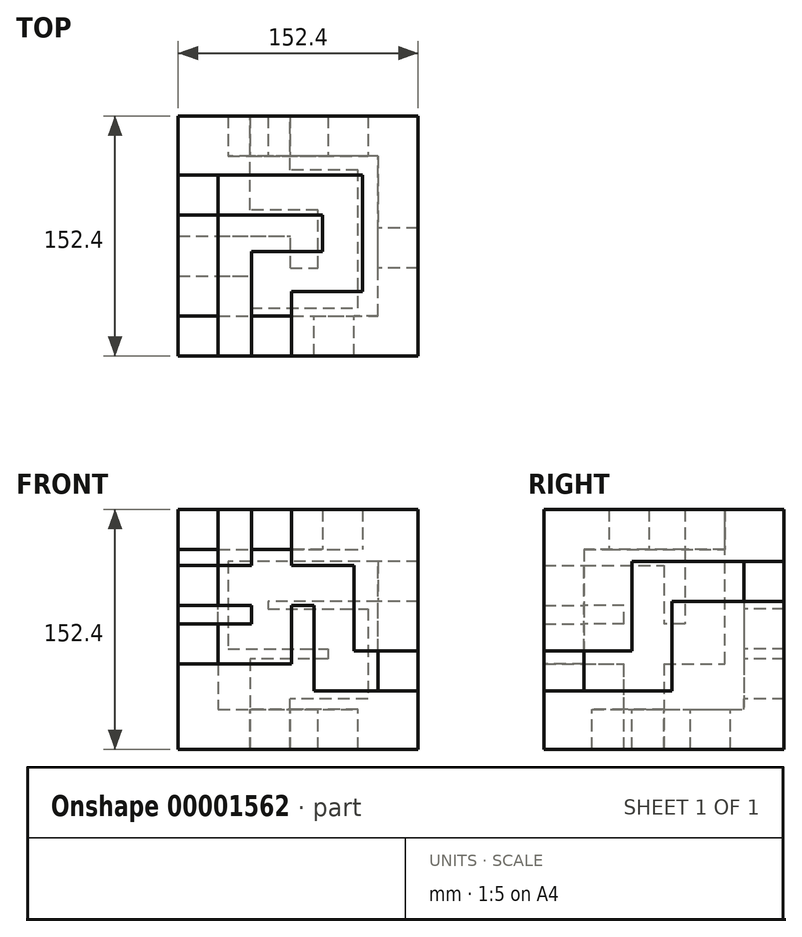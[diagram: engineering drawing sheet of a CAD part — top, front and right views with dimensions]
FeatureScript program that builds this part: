
annotation { "Feature Type Name" : "Feature", "Feature Type Description" : "" }
export const myFeature = defineFeature(function(context is Context, id is Id, definition is map)
    precondition{}
    {
        {
            var Q0;
            Q0=qCreatedBy(makeId("Top.planeOp"),FACE);
            var sketch = newSketch(context, id + "F0", { "sketchPlane" : qUnion([Q0])});
            skLineSegment(sketch, "E0.rect.bottom", {"start": v(-50.8, 50.8) * mm, "end": v(50.8, 50.8) * mm});
            skLineSegment(sketch, "E0.rect.top", {"start": v(-50.8, -50.8) * mm, "end": v(50.8, -50.8) * mm});
            skLineSegment(sketch, "E0.rect.left", {"start": v(-50.8, 50.8) * mm, "end": v(-50.8, -50.8) * mm});
            skLineSegment(sketch, "E0.rect.right", {"start": v(50.8, 50.8) * mm, "end": v(50.8, -50.8) * mm});
            skPoint(sketch, "E0.rect.middle", {"position": v(0, 0) * mm});
            skSolve(sketch);
        }
        {
            var Q0;
            Q0=makeQuery(id+"F0.imprint","IMPRINT",FACE,{"disambiguationData":[TD([[makeQuery(id+"F0.imprint","IMPRINT",EDGE,{"derivedFrom":sQuery(id+"F0.wireOp",EDGE,"E0.rect.bottom")}),-1.0]])]});
            extrude(context, id + "F1", {"entities" : qUnion([Q0]), "endBound" : BoundingType.SYMMETRIC, "depth" : 101.6 * mm});
        }
        {
            var Q0;
            Q0=makeQuery(id+"F1.opExtrude","CAP_FACE",FACE,{"disambiguationData":[OSD([sQuery(id+"F0.wireOp",EDGE,"E0.rect.bottom"),sQuery(id+"F0.wireOp",EDGE,"E0.rect.top"),sQuery(id+"F0.wireOp",EDGE,"E0.rect.left"),sQuery(id+"F0.wireOp",EDGE,"E0.rect.right")])],"isStart":false});
            var sketch = newSketch(context, id + "F2", { "sketchPlane" : qUnion([Q0])});
            skLineSegment(sketch, "E1", {"start": v(15.5, 13.25) * mm, "end": v(15.5, -9.7) * mm});
            skLineSegment(sketch, "E2", {"start": v(15.5, -9.7) * mm, "end": v(-29.46, -9.7) * mm});
            skLineSegment(sketch, "E3", {"start": v(-29.46, -9.7) * mm, "end": v(-29.46, -50.8) * mm});
            skLineSegment(sketch, "E4", {"start": v(-29.46, -50.8) * mm, "end": v(-4.06, -50.8) * mm});
            skLineSegment(sketch, "E5", {"start": v(-4.06, -50.8) * mm, "end": v(-4.06, -35.1) * mm});
            skLineSegment(sketch, "E6", {"start": v(-4.06, -35.1) * mm, "end": v(40.9, -35.1) * mm});
            skLineSegment(sketch, "E7", {"start": v(40.9, -35.1) * mm, "end": v(40.9, 38.65) * mm});
            skLineSegment(sketch, "E8.bottom", {"start": v(-50.8, 38.65) * mm, "end": v(40.9, 38.65) * mm});
            skLineSegment(sketch, "E8.top", {"start": v(-50.8, 13.25) * mm, "end": v(15.5, 13.25) * mm});
            skLineSegment(sketch, "E8.left", {"start": v(-50.8, 38.65) * mm, "end": v(-50.8, 13.25) * mm});
            skSolve(sketch);
        }
        {
            var Q0;
            Q0=makeQuery(id+"F1.opExtrude","SWEPT_FACE",FACE,{"disambiguationData":[OSD([sQuery(id+"F0.wireOp",EDGE,"E0.rect.left")])]});
            var sketch = newSketch(context, id + "F3", { "sketchPlane" : qUnion([Q0])});
            skLineSegment(sketch, "E9", {"start": v(-13.26, 50.8) * mm, "end": v(-13.26, 3.6) * mm});
            skLineSegment(sketch, "E10", {"start": v(-13.26, 3.6) * mm, "end": v(50.8, 3.6) * mm});
            skLineSegment(sketch, "E11", {"start": v(50.8, 3.6) * mm, "end": v(50.8, -21.8) * mm});
            skLineSegment(sketch, "E12", {"start": v(50.8, -21.8) * mm, "end": v(-38.66, -21.8) * mm});
            skLineSegment(sketch, "E13", {"start": v(-38.66, -21.8) * mm, "end": v(-38.66, 50.8) * mm});
            skLineSegment(sketch, "E14", {"start": v(50.8, 40.7) * mm, "end": v(0, 40.7) * mm});
            skLineSegment(sketch, "E15", {"start": v(0, 40.7) * mm, "end": v(0, -50.8) * mm});
            skLineSegment(sketch, "E16", {"start": v(0, -50.8) * mm, "end": v(25.4, -50.8) * mm});
            skLineSegment(sketch, "E17", {"start": v(25.4, -50.8) * mm, "end": v(25.4, 15.3) * mm});
            skLineSegment(sketch, "E18", {"start": v(25.4, 15.3) * mm, "end": v(50.8, 15.3) * mm});
            skSolve(sketch);
        }
        {
            var Q0;
            Q0=makeQuery(id+"F1.opExtrude","SWEPT_FACE",FACE,{"disambiguationData":[OSD([sQuery(id+"F0.wireOp",EDGE,"E0.rect.top")])]});
            var sketch = newSketch(context, id + "F4", { "sketchPlane" : qUnion([Q0])});
            skLineSegment(sketch, "E19", {"start": v(-29.46, 50.8) * mm, "end": v(-29.46, 3.6) * mm});
            skLineSegment(sketch, "E20", {"start": v(-4.06, 50.8) * mm, "end": v(-4.06, 11.87) * mm});
            skLineSegment(sketch, "E21", {"start": v(-29.46, 3.6) * mm, "end": v(-50.8, 3.6) * mm});
            skLineSegment(sketch, "E22", {"start": v(-50.8, -21.8) * mm, "end": v(-4.06, -21.8) * mm});
            skLineSegment(sketch, "E23", {"start": v(-4.06, 11.87) * mm, "end": v(-4.06, -21.8) * mm});
            skLineSegment(sketch, "E24", {"start": v(-50.8, 40.7) * mm, "end": v(10.18, 40.7) * mm});
            skLineSegment(sketch, "E25", {"start": v(-50.8, 15.3) * mm, "end": v(10.18, 15.3) * mm});
            skLineSegment(sketch, "E26", {"start": v(10.18, 15.3) * mm, "end": v(10.18, -38.9) * mm});
            skLineSegment(sketch, "E27", {"start": v(10.18, -38.9) * mm, "end": v(50.8, -38.9) * mm});
            skLineSegment(sketch, "E28", {"start": v(50.8, -38.9) * mm, "end": v(50.8, -13.5) * mm});
            skLineSegment(sketch, "E29", {"start": v(50.8, -13.5) * mm, "end": v(35.58, -13.5) * mm});
            skLineSegment(sketch, "E30", {"start": v(35.58, -13.5) * mm, "end": v(35.58, 40.7) * mm});
            skLineSegment(sketch, "E31", {"start": v(35.58, 40.7) * mm, "end": v(10.18, 40.7) * mm});
            skSolve(sketch);
        }
        {
            var Q0;
            Q0=makeQuery(id+"F1.opExtrude","CAP_FACE",FACE,{"disambiguationData":[OSD([sQuery(id+"F0.wireOp",EDGE,"E0.rect.bottom"),sQuery(id+"F0.wireOp",EDGE,"E0.rect.top"),sQuery(id+"F0.wireOp",EDGE,"E0.rect.left"),sQuery(id+"F0.wireOp",EDGE,"E0.rect.right")])],"isStart":true});
            var sketch = newSketch(context, id + "F5", { "sketchPlane" : qUnion([Q0])});
            skLineSegment(sketch, "E32", {"start": v(-50.8, 25.4) * mm, "end": v(-30.37, 25.4) * mm});
            skLineSegment(sketch, "E33", {"start": v(-50.8, 0) * mm, "end": v(-30.37, 0) * mm});
            skLineSegment(sketch, "E34", {"start": v(-4.97, 20.26) * mm, "end": v(-4.97, 0) * mm});
            skLineSegment(sketch, "E35", {"start": v(-4.97, 0) * mm, "end": v(-30.37, 0) * mm});
            skLineSegment(sketch, "E36", {"start": v(-30.37, 25.4) * mm, "end": v(-30.37, 45.66) * mm});
            skLineSegment(sketch, "E37", {"start": v(-30.37, 45.66) * mm, "end": v(37.93, 45.66) * mm});
            skLineSegment(sketch, "E38", {"start": v(37.93, 45.66) * mm, "end": v(37.93, -16.62) * mm});
            skLineSegment(sketch, "E39", {"start": v(-4.97, 20.26) * mm, "end": v(12.53, 20.26) * mm});
            skLineSegment(sketch, "E40", {"start": v(12.53, 20.26) * mm, "end": v(12.53, -16.62) * mm});
            skLineSegment(sketch, "E41", {"start": v(37.93, -16.62) * mm, "end": v(37.93, -42.02) * mm});
            skLineSegment(sketch, "E42", {"start": v(37.93, -42.02) * mm, "end": v(-5.04, -42.02) * mm});
            skLineSegment(sketch, "E43", {"start": v(-5.04, -42.02) * mm, "end": v(-5.04, -50.8) * mm});
            skLineSegment(sketch, "E44", {"start": v(12.53, -16.62) * mm, "end": v(-30.44, -16.62) * mm});
            skLineSegment(sketch, "E45", {"start": v(-30.44, -16.62) * mm, "end": v(-30.44, -50.8) * mm});
            skSolve(sketch);
        }
        {
            var Q0;
            Q0=makeQuery(id+"F1.opExtrude","SWEPT_FACE",FACE,{"disambiguationData":[OSD([sQuery(id+"F0.wireOp",EDGE,"E0.rect.right")])]});
            var sketch = newSketch(context, id + "F6", { "sketchPlane" : qUnion([Q0])});
            skLineSegment(sketch, "E46", {"start": v(-50.8, -13.49) * mm, "end": v(-40.23, -13.49) * mm});
            skLineSegment(sketch, "E47", {"start": v(-50.8, -38.89) * mm, "end": v(-40.23, -38.89) * mm});
            skLineSegment(sketch, "E48", {"start": v(50.8, 43.06) * mm, "end": v(42.8, 43.06) * mm});
            skLineSegment(sketch, "E49", {"start": v(50.8, 17.66) * mm, "end": v(42.8, 17.66) * mm});
            skLineSegment(sketch, "E50", {"start": v(-40.23, -13.49) * mm, "end": v(-20.3, -13.49) * mm});
            skLineSegment(sketch, "E51", {"start": v(-20.3, -13.49) * mm, "end": v(-20.3, 43.06) * mm});
            skLineSegment(sketch, "E52", {"start": v(-20.3, 43.06) * mm, "end": v(42.8, 43.06) * mm});
            skLineSegment(sketch, "E53", {"start": v(-40.23, -38.89) * mm, "end": v(5.1, -38.89) * mm});
            skLineSegment(sketch, "E54", {"start": v(5.1, -38.89) * mm, "end": v(5.1, 17.66) * mm});
            skLineSegment(sketch, "E55", {"start": v(5.1, 17.66) * mm, "end": v(42.8, 17.66) * mm});
            skSolve(sketch);
        }
        {
            var Q0;
            Q0=makeQuery(id+"F1.opExtrude","SWEPT_FACE",FACE,{"disambiguationData":[OSD([sQuery(id+"F0.wireOp",EDGE,"E0.rect.bottom")])]});
            var sketch = newSketch(context, id + "F7", { "sketchPlane" : qUnion([Q0])});
            skLineSegment(sketch, "E56", {"start": v(-50.8, 43.06) * mm, "end": v(-41.8, 43.06) * mm});
            skLineSegment(sketch, "E57", {"start": v(-50.8, 17.66) * mm, "end": v(-41.8, 17.66) * mm});
            skLineSegment(sketch, "E58", {"start": v(30.44, -50.8) * mm, "end": v(30.44, -44.27) * mm});
            skLineSegment(sketch, "E59", {"start": v(5.04, -50.8) * mm, "end": v(5.04, -44.27) * mm});
            skLineSegment(sketch, "E60", {"start": v(-41.8, 17.66) * mm, "end": v(19.26, 17.66) * mm});
            skLineSegment(sketch, "E61", {"start": v(19.26, 17.66) * mm, "end": v(19.26, 13.19) * mm});
            skLineSegment(sketch, "E62", {"start": v(19.26, 13.19) * mm, "end": v(-44.22, 13.19) * mm});
            skLineSegment(sketch, "E63", {"start": v(-44.22, 13.19) * mm, "end": v(-44.22, -44.27) * mm});
            skLineSegment(sketch, "E64", {"start": v(-44.22, -44.27) * mm, "end": v(5.04, -44.27) * mm});
            skLineSegment(sketch, "E65", {"start": v(-41.8, 43.06) * mm, "end": v(44.66, 43.06) * mm});
            skLineSegment(sketch, "E66", {"start": v(44.66, 43.06) * mm, "end": v(44.66, -12.21) * mm});
            skLineSegment(sketch, "E67", {"start": v(44.66, -12.21) * mm, "end": v(-18.82, -12.21) * mm});
            skLineSegment(sketch, "E68", {"start": v(-18.82, -12.21) * mm, "end": v(-18.82, -18.87) * mm});
            skLineSegment(sketch, "E69", {"start": v(-18.82, -18.87) * mm, "end": v(30.44, -18.87) * mm});
            skLineSegment(sketch, "E70", {"start": v(30.44, -18.87) * mm, "end": v(30.44, -44.27) * mm});
            skSolve(sketch);
        }
        {
            var Q0;
            {var subQ2=sQuery(id+"F7.wireOp",EDGE,"E56");Q0=makeQuery(id+"F7.imprint","IMPRINT",FACE,{"disambiguationData":[TD([[makeQuery(id+"F7.imprint","IMPRINT",EDGE,{"derivedFrom":subQ2}),1.0]])]});}
            var Q1;
            {var subQ5=sQuery(id+"F7.wireOp",EDGE,"E57");Q1=makeQuery(id+"F7.imprint","IMPRINT",FACE,{"disambiguationData":[TD([[makeQuery(id+"F7.imprint","IMPRINT",EDGE,{"derivedFrom":subQ5}),-1.0]])]});}
            extrude(context, id + "F8", {"entities" : qUnion([Q0, Q1]), "operationType" : NewBodyOperationType.ADD, "depth" : 25.4 * mm});
        }
        {
            var Q0;
            {var subQ2=sQuery(id+"F6.wireOp",EDGE,"E47");Q0=makeQuery(id+"F6.imprint","IMPRINT",FACE,{"disambiguationData":[TD([[makeQuery(id+"F6.imprint","IMPRINT",EDGE,{"derivedFrom":subQ2}),-1.0]])]});}
            var Q1;
            {var subQ2=sQuery(id+"F6.wireOp",EDGE,"E46");Q1=makeQuery(id+"F6.imprint","IMPRINT",FACE,{"disambiguationData":[TD([[makeQuery(id+"F6.imprint","IMPRINT",EDGE,{"derivedFrom":subQ2}),1.0]])]});}
            extrude(context, id + "F9", {"entities" : qUnion([Q0, Q1]), "operationType" : NewBodyOperationType.ADD, "depth" : 25.4 * mm});
        }
        {
            var Q0;
            {var subQ5=sQuery(id+"F4.wireOp",EDGE,"E22");Q0=makeQuery(id+"F4.imprint","IMPRINT",FACE,{"disambiguationData":[TD([[makeQuery(id+"F4.imprint","IMPRINT",EDGE,{"derivedFrom":subQ5}),-1.0]])]});}
            var Q1;
            {var subQ7=sQuery(id+"F4.wireOp",EDGE,"E29");Q1=makeQuery(id+"F4.imprint","IMPRINT",FACE,{"disambiguationData":[TD([[makeQuery(id+"F4.imprint","IMPRINT",EDGE,{"derivedFrom":subQ7}),-1.0]])]});}
            var Q2;
            {var subQ3=sQuery(id+"F4.wireOp",EDGE,"E21");Q2=makeQuery(id+"F4.imprint","IMPRINT",FACE,{"disambiguationData":[TD([[makeQuery(id+"F4.imprint","IMPRINT",EDGE,{"derivedFrom":subQ3}),-1.0]])]});}
            var Q3;
            {var subQ0=sQuery(id+"F0.wireOp",EDGE,"E0.rect.top");var subQ1=makeQuery(id+"F1.opExtrude","CAP_EDGE",EDGE,{"disambiguationData":[OSD([subQ0])],"isStart":false});var subQ2=sQuery(id+"F4.wireOp",EDGE,"E19");var subQ3=makeQuery(id+"F4.imprint","INTERSECT",VERTEX,{"derivedFrom":[subQ1,subQ2]});Q3=makeQuery(id+"F4.imprint","IMPRINT",FACE,{"disambiguationData":[TD([[makeQuery(id+"F4.imprint","IMPRINT",EDGE,{"disambiguationData":[TD([[subQ3,-1.0]])],"derivedFrom":subQ2}),-1.0]])]});}
            extrude(context, id + "F10", {"entities" : qUnion([Q0, Q1, Q2, Q3]), "operationType" : NewBodyOperationType.ADD, "depth" : 25.4 * mm});
        }
        {
            var Q0;
            {var subQ1=sQuery(id+"F3.wireOp",EDGE,"E18");Q0=makeQuery(id+"F3.imprint","IMPRINT",FACE,{"disambiguationData":[TD([[makeQuery(id+"F3.imprint","IMPRINT",EDGE,{"derivedFrom":subQ1}),-1.0]])]});}
            var Q1;
            {var subQ2=sQuery(id+"F3.wireOp",EDGE,"E17");var subQ6=sQuery(id+"F3.wireOp",EDGE,"E12");var subQ8=makeQuery(id+"F3.imprint","INTERSECT",VERTEX,{"derivedFrom":[subQ6,subQ2]});Q1=makeQuery(id+"F3.imprint","IMPRINT",FACE,{"disambiguationData":[TD([[makeQuery(id+"F3.imprint","IMPRINT",EDGE,{"disambiguationData":[TD([[subQ8,1.0]])],"derivedFrom":subQ2}),-1.0]])]});}
            var Q2;
            {var subQ2=sQuery(id+"F3.wireOp",EDGE,"E9");Q2=makeQuery(id+"F3.imprint","IMPRINT",FACE,{"disambiguationData":[TD([[makeQuery(id+"F3.imprint","IMPRINT",EDGE,{"derivedFrom":subQ2}),1.0]])]});}
            var Q3;
            {var subQ2=sQuery(id+"F3.wireOp",EDGE,"E13");Q3=makeQuery(id+"F3.imprint","IMPRINT",FACE,{"disambiguationData":[TD([[makeQuery(id+"F3.imprint","IMPRINT",EDGE,{"derivedFrom":subQ2}),1.0]])]});}
            extrude(context, id + "F11", {"entities" : qUnion([Q0, Q1, Q2, Q3]), "operationType" : NewBodyOperationType.ADD, "depth" : 25.4 * mm});
        }
        {
            var Q0;
            {var subQ4=sQuery(id+"F2.wireOp",EDGE,"E5");Q0=makeQuery(id+"F2.imprint","IMPRINT",FACE,{"disambiguationData":[TD([[makeQuery(id+"F2.imprint","IMPRINT",EDGE,{"derivedFrom":subQ4}),-1.0]])]});}
            var Q1;
            Q1=makeQuery(id+"F2.imprint","IMPRINT",FACE,{"disambiguationData":[TD([[makeQuery(id+"F2.imprint","IMPRINT",EDGE,{"derivedFrom":sQuery(id+"F2.wireOp",EDGE,"E1")}),-1.0]])]});
            extrude(context, id + "F12", {"entities" : qUnion([Q0, Q1]), "operationType" : NewBodyOperationType.ADD, "depth" : 25.4 * mm});
        }
        {
            var Q0;
            {var subQ1=sQuery(id+"F5.wireOp",EDGE,"E32");Q0=makeQuery(id+"F5.imprint","IMPRINT",FACE,{"disambiguationData":[TD([[makeQuery(id+"F5.imprint","IMPRINT",EDGE,{"derivedFrom":subQ1}),1.0]])]});}
            var Q1;
            {var subQ1=sQuery(id+"F5.wireOp",EDGE,"E33");Q1=makeQuery(id+"F5.imprint","IMPRINT",FACE,{"disambiguationData":[TD([[makeQuery(id+"F5.imprint","IMPRINT",EDGE,{"derivedFrom":subQ1}),-1.0]])]});}
            extrude(context, id + "F13", {"entities" : qUnion([Q0, Q1]), "operationType" : NewBodyOperationType.ADD, "depth" : 25.4 * mm});
        }
        {
            var Q0;
            Q0=makeQuery(id+"F13.opExtrude","SWEPT_FACE",FACE,{"disambiguationData":[OSD([sQuery(id+"F0.wireOp",EDGE,"E0.rect.right")])]});
            var sketch = newSketch(context, id + "F14", { "sketchPlane" : qUnion([Q0])});
            skLineSegment(sketch, "E71.bottom", {"start": v(50.8, -76.2) * mm, "end": v(-50.8, -76.2) * mm});
            skLineSegment(sketch, "E71.top", {"start": v(50.8, -50.8) * mm, "end": v(-50.8, -50.8) * mm});
            skLineSegment(sketch, "E71.left", {"start": v(50.8, -76.2) * mm, "end": v(50.8, -50.8) * mm});
            skLineSegment(sketch, "E71.right", {"start": v(-50.8, -76.2) * mm, "end": v(-50.8, -50.8) * mm});
            skSolve(sketch);
        }
        {
            var Q0;
            Q0=makeQuery(id+"F14.imprint","IMPRINT",FACE,{"disambiguationData":[TD([[makeQuery(id+"F14.imprint","IMPRINT",EDGE,{"derivedFrom":sQuery(id+"F14.wireOp",EDGE,"E71.bottom")}),-1.0]])]});
            extrude(context, id + "F15", {"entities" : qUnion([Q0]), "operationType" : NewBodyOperationType.ADD, "depth" : 25.4 * mm});
        }
        {
            var Q0;
            {var subQ0=sQuery(id+"F0.wireOp",EDGE,"E0.rect.top");var subQ1=sQuery(id+"F0.wireOp",EDGE,"E0.rect.right");var subQ2=makeQuery(id+"F1.opExtrude","SWEPT_EDGE",EDGE,{"disambiguationData":[OSD([subQ0,subQ1])]});Q0=makeQuery(id+"F10.opExtrude","SWEPT_FACE",FACE,{"disambiguationData":[OSD([subQ0,subQ1]),TDD([makeQuery(id+"F4.imprint","IMPRINT",EDGE,{"disambiguationData":[TD([[makeQuery(id+"F4.imprint","INTERSECT",VERTEX,{"derivedFrom":[subQ2,makeQuery(id+"F1.opExtrude","CAP_EDGE",EDGE,{"disambiguationData":[OSD([subQ0])],"isStart":true})]}),1.0]])],"derivedFrom":subQ2})])]});}
            var sketch = newSketch(context, id + "F16", { "sketchPlane" : qUnion([Q0])});
            skLineSegment(sketch, "E72.bottom", {"start": v(-50.8, -50.8) * mm, "end": v(-76.2, -50.8) * mm});
            skLineSegment(sketch, "E72.top", {"start": v(-50.8, -38.9) * mm, "end": v(-76.2, -38.9) * mm});
            skLineSegment(sketch, "E72.left", {"start": v(-50.8, -50.8) * mm, "end": v(-50.8, -38.9) * mm});
            skLineSegment(sketch, "E72.right", {"start": v(-76.2, -50.8) * mm, "end": v(-76.2, -38.9) * mm});
            skSolve(sketch);
        }
        {
            var Q0;
            Q0=makeQuery(id+"F16.imprint","IMPRINT",FACE,{"disambiguationData":[TD([[makeQuery(id+"F16.imprint","IMPRINT",EDGE,{"derivedFrom":sQuery(id+"F16.wireOp",EDGE,"E72.bottom")}),1.0]])]});
            extrude(context, id + "F17", {"entities" : qUnion([Q0]), "operationType" : NewBodyOperationType.ADD, "depth" : 25.4 * mm});
        }
        {
            var Q0;
            {var subQ0=sQuery(id+"F0.wireOp",EDGE,"E0.rect.top");var subQ1=sQuery(id+"F0.wireOp",EDGE,"E0.rect.right");var subQ2=makeQuery(id+"F1.opExtrude","SWEPT_EDGE",EDGE,{"disambiguationData":[OSD([subQ0,subQ1])]});var subQ3=sQuery(id+"F6.wireOp",EDGE,"E46");var subQ4=makeQuery(id+"F1.opExtrude","CAP_EDGE",EDGE,{"disambiguationData":[OSD([subQ1])],"isStart":false});var subQ8=sQuery(id+"F6.wireOp",EDGE,"E50");Q0=makeQuery(id+"F10.boolean.opBoolean","SPLIT",FACE,{"disambiguationData":[TD([makeQuery(id+"F9.opExtrude","SWEPT_FACE",FACE,{"disambiguationData":[OSD([subQ3,subQ8])]})])],"derivedFrom":makeQuery(id+"F9.boolean.opBoolean","MERGE",FACE,{"derivedFrom":[makeQuery(id+"F1.opExtrude","SWEPT_FACE",FACE,{"disambiguationData":[OSD([subQ0])]}),makeQuery(id+"F9.opExtrude","SWEPT_FACE",FACE,{"disambiguationData":[OSD([subQ0,subQ1]),TDD([makeQuery(id+"F6.imprint","IMPRINT",EDGE,{"disambiguationData":[TD([[makeQuery(id+"F6.imprint","INTERSECT",VERTEX,{"derivedFrom":[subQ2,makeQuery(id+"F1.opExtrude","CAP_EDGE",EDGE,{"disambiguationData":[OSD([subQ1])],"isStart":true})]}),1.0]])],"derivedFrom":subQ2})])]}),makeQuery(id+"F9.opExtrude","SWEPT_FACE",FACE,{"disambiguationData":[OSD([subQ0,subQ1]),TDD([makeQuery(id+"F6.imprint","IMPRINT",EDGE,{"disambiguationData":[TD([[makeQuery(id+"F6.imprint","INTERSECT",VERTEX,{"derivedFrom":[subQ2,subQ4]}),-1.0]])],"derivedFrom":subQ2})])]})]})});}
            var sketch = newSketch(context, id + "F18", { "sketchPlane" : qUnion([Q0])});
            skLineSegment(sketch, "E73.bottom", {"start": v(76.2, 50.8) * mm, "end": v(50.8, 50.8) * mm});
            skLineSegment(sketch, "E73.top", {"start": v(76.2, -13.49) * mm, "end": v(50.8, -13.49) * mm});
            skLineSegment(sketch, "E73.left", {"start": v(76.2, 50.8) * mm, "end": v(76.2, -13.49) * mm});
            skLineSegment(sketch, "E73.right", {"start": v(50.8, 50.8) * mm, "end": v(50.8, -13.49) * mm});
            skSolve(sketch);
        }
        {
            var Q0;
            Q0=makeQuery(id+"F18.imprint","IMPRINT",FACE,{"disambiguationData":[TD([[makeQuery(id+"F18.imprint","IMPRINT",EDGE,{"derivedFrom":sQuery(id+"F18.wireOp",EDGE,"E73.bottom")}),-1.0]])]});
            extrude(context, id + "F19", {"entities" : qUnion([Q0]), "operationType" : NewBodyOperationType.ADD, "depth" : 25.4 * mm});
        }
        {
            var Q0;
            {var subQ0=sQuery(id+"F0.wireOp",EDGE,"E0.rect.bottom");var subQ1=sQuery(id+"F0.wireOp",EDGE,"E0.rect.right");var subQ2=makeQuery(id+"F1.opExtrude","SWEPT_EDGE",EDGE,{"disambiguationData":[OSD([subQ0,subQ1])]});var subQ3=makeQuery(id+"F1.opExtrude","CAP_EDGE",EDGE,{"disambiguationData":[OSD([subQ1])],"isStart":true});var subQ4=makeQuery(id+"F1.opExtrude","CAP_EDGE",EDGE,{"disambiguationData":[OSD([subQ0])],"isStart":true});Q0=makeQuery(id+"F15.boolean.opBoolean","MERGE",FACE,{"derivedFrom":[makeQuery(id+"F13.boolean.opBoolean","MERGE",FACE,{"derivedFrom":[makeQuery(id+"F9.boolean.opBoolean","MERGE",FACE,{"derivedFrom":[makeQuery(id+"F1.opExtrude","SWEPT_FACE",FACE,{"disambiguationData":[OSD([subQ0])]}),makeQuery(id+"F9.opExtrude","SWEPT_FACE",FACE,{"disambiguationData":[OSD([subQ0,subQ1]),TDD([makeQuery(id+"F6.imprint","IMPRINT",EDGE,{"disambiguationData":[TD([[makeQuery(id+"F6.imprint","INTERSECT",VERTEX,{"derivedFrom":[subQ2,subQ3]}),1.0]])],"derivedFrom":subQ2})])]})]}),makeQuery(id+"F13.opExtrude","SWEPT_FACE",FACE,{"disambiguationData":[OSD([subQ0]),TDD([makeQuery(id+"F5.imprint","IMPRINT",EDGE,{"disambiguationData":[TD([[makeQuery(id+"F5.imprint","INTERSECT",VERTEX,{"derivedFrom":[subQ4,subQ3]}),1.0]])],"derivedFrom":subQ4})])]})]}),makeQuery(id+"F15.opExtrude","SWEPT_FACE",FACE,{"disambiguationData":[OSD([sQuery(id+"F14.wireOp",EDGE,"E71.left")])]})]});}
            var sketch = newSketch(context, id + "F20", { "sketchPlane" : qUnion([Q0])});
            skLineSegment(sketch, "E74.bottom", {"start": v(-76.2, 17.66) * mm, "end": v(-50.8, 17.66) * mm});
            skLineSegment(sketch, "E74.top", {"start": v(-76.2, -76.2) * mm, "end": v(-50.8, -76.2) * mm});
            skLineSegment(sketch, "E74.left", {"start": v(-76.2, 17.66) * mm, "end": v(-76.2, -76.2) * mm});
            skLineSegment(sketch, "E74.right", {"start": v(-50.8, 17.66) * mm, "end": v(-50.8, -50.8) * mm});
            skLineSegment(sketch, "E75.bottom", {"start": v(-50.8, -50.8) * mm, "end": v(5.04, -50.8) * mm});
            skLineSegment(sketch, "E75.top", {"start": v(-50.8, -76.2) * mm, "end": v(5.04, -76.2) * mm});
            skLineSegment(sketch, "E75.right", {"start": v(5.04, -50.8) * mm, "end": v(5.04, -76.2) * mm});
            skSolve(sketch);
        }
        {
            var Q0;
            {var subQ7=sQuery(id+"F20.wireOp",EDGE,"E74.bottom");Q0=makeQuery(id+"F20.imprint","IMPRINT",FACE,{"disambiguationData":[TD([[makeQuery(id+"F20.imprint","IMPRINT",EDGE,{"derivedFrom":subQ7}),-1.0]])]});}
            extrude(context, id + "F21", {"entities" : qUnion([Q0]), "operationType" : NewBodyOperationType.ADD, "depth" : 25.4 * mm});
        }
        {
            var Q0;
            {var subQ0=sQuery(id+"F0.wireOp",EDGE,"E0.rect.bottom");var subQ1=sQuery(id+"F0.wireOp",EDGE,"E0.rect.top");var subQ2=sQuery(id+"F0.wireOp",EDGE,"E0.rect.left");var subQ3=sQuery(id+"F0.wireOp",EDGE,"E0.rect.right");var subQ4=makeQuery(id+"F1.opExtrude","CAP_FACE",FACE,{"disambiguationData":[OSD([subQ0,subQ1,subQ2,subQ3])],"isStart":false});var subQ5=makeQuery(id+"F1.opExtrude","CAP_EDGE",EDGE,{"disambiguationData":[OSD([subQ0])],"isStart":false});var subQ6=makeQuery(id+"F8.opExtrude","SWEPT_FACE",FACE,{"disambiguationData":[OSD([subQ0]),TDD([makeQuery(id+"F7.imprint","IMPRINT",EDGE,{"derivedFrom":subQ5})])]});var subQ7=makeQuery(id+"F1.opExtrude","CAP_EDGE",EDGE,{"disambiguationData":[OSD([subQ3])],"isStart":false});var subQ8=makeQuery(id+"F9.opExtrude","SWEPT_FACE",FACE,{"disambiguationData":[OSD([subQ3]),TDD([makeQuery(id+"F6.imprint","IMPRINT",EDGE,{"derivedFrom":subQ7})])]});var subQ9=makeQuery(id+"F1.opExtrude","CAP_EDGE",EDGE,{"disambiguationData":[OSD([subQ1])],"isStart":false});var subQ11=makeQuery(id+"F10.opExtrude","SWEPT_FACE",FACE,{"disambiguationData":[OSD([subQ1]),TDD([makeQuery(id+"F4.imprint","IMPRINT",EDGE,{"disambiguationData":[TD([[makeQuery(id+"F4.imprint","INTERSECT",VERTEX,{"derivedFrom":[subQ9,sQuery(id+"F4.wireOp",EDGE,"E19")]}),1.0]])],"derivedFrom":subQ9})])]});var subQ12=sQuery(id+"F4.wireOp",EDGE,"E20");var subQ15=makeQuery(id+"F10.opExtrude","SWEPT_FACE",FACE,{"disambiguationData":[OSD([subQ1]),TDD([makeQuery(id+"F4.imprint","IMPRINT",EDGE,{"disambiguationData":[TD([[makeQuery(id+"F4.imprint","INTERSECT",VERTEX,{"derivedFrom":[subQ9,subQ12]}),-1.0]])],"derivedFrom":subQ9})])]});var subQ16=makeQuery(id+"F1.opExtrude","CAP_EDGE",EDGE,{"disambiguationData":[OSD([subQ2])],"isStart":false});var subQ17=makeQuery(id+"F11.opExtrude","SWEPT_FACE",FACE,{"disambiguationData":[OSD([subQ2]),TDD([makeQuery(id+"F3.imprint","IMPRINT",EDGE,{"disambiguationData":[TD([[makeQuery(id+"F3.imprint","INTERSECT",VERTEX,{"derivedFrom":[subQ16,sQuery(id+"F3.wireOp",EDGE,"E13")]}),1.0]])],"derivedFrom":subQ16})])]});var subQ18=makeQuery(id+"F11.opExtrude","SWEPT_FACE",FACE,{"disambiguationData":[OSD([subQ2]),TDD([makeQuery(id+"F3.imprint","IMPRINT",EDGE,{"disambiguationData":[TD([[makeQuery(id+"F3.imprint","INTERSECT",VERTEX,{"derivedFrom":[subQ16,sQuery(id+"F3.wireOp",EDGE,"E9")]}),-1.0]])],"derivedFrom":subQ16})])]});var subQ19=makeQuery(id+"F11.boolean.opBoolean","MERGE",FACE,{"derivedFrom":[makeQuery(id+"F10.boolean.opBoolean","MERGE",FACE,{"derivedFrom":[makeQuery(id+"F9.boolean.opBoolean","MERGE",FACE,{"derivedFrom":[makeQuery(id+"F8.boolean.opBoolean","MERGE",FACE,{"derivedFrom":[subQ4,subQ6]}),subQ8]}),subQ11,subQ15]}),subQ17,subQ18]});var subQ21=sQuery(id+"F6.wireOp",EDGE,"E46");var subQ25=sQuery(id+"F6.wireOp",EDGE,"E48");var subQ30=sQuery(id+"F4.wireOp",EDGE,"E29");Q0=makeQuery(id+"F19.boolean.opBoolean","MERGE",FACE,{"derivedFrom":[makeQuery(id+"F12.boolean.opBoolean","SPLIT",FACE,{"disambiguationData":[TD([makeQuery(id+"F9.opExtrude","CAP_FACE",FACE,{"disambiguationData":[OSD([subQ0,subQ1,subQ3,subQ21,subQ25,sQuery(id+"F6.wireOp",EDGE,"E50"),sQuery(id+"F6.wireOp",EDGE,"E51"),sQuery(id+"F6.wireOp",EDGE,"E52")])],"isStart":false})])],"derivedFrom":subQ19}),makeQuery(id+"F12.boolean.opBoolean","SPLIT",FACE,{"disambiguationData":[TD([makeQuery(id+"F10.opExtrude","CAP_FACE",FACE,{"disambiguationData":[OSD([subQ1,subQ3,subQ12,sQuery(id+"F4.wireOp",EDGE,"E24"),subQ30,sQuery(id+"F4.wireOp",EDGE,"E30"),sQuery(id+"F4.wireOp",EDGE,"E31")])],"isStart":false})])],"derivedFrom":subQ19}),makeQuery(id+"F19.opExtrude","SWEPT_FACE",FACE,{"disambiguationData":[OSD([sQuery(id+"F18.wireOp",EDGE,"E73.bottom")])]})]});}
            var sketch = newSketch(context, id + "F22", { "sketchPlane" : qUnion([Q0])});
            skLineSegment(sketch, "E76", {"start": v(50.8, 50.8) * mm, "end": v(76.2, 50.8) * mm});
            skLineSegment(sketch, "E77", {"start": v(76.2, 50.8) * mm, "end": v(76.2, -76.2) * mm});
            skLineSegment(sketch, "E78", {"start": v(76.2, -76.2) * mm, "end": v(-4.06, -76.2) * mm});
            skLineSegment(sketch, "E79", {"start": v(-4.06, -76.2) * mm, "end": v(-4.06, -50.8) * mm});
            skLineSegment(sketch, "E80", {"start": v(-4.06, -50.8) * mm, "end": v(50.8, -50.8) * mm});
            skLineSegment(sketch, "E81", {"start": v(50.8, -50.8) * mm, "end": v(50.8, 50.8) * mm});
            skSolve(sketch);
        }
        {
            var Q0;
            Q0=makeQuery(id+"F22.imprint","IMPRINT",FACE,{"disambiguationData":[TD([[makeQuery(id+"F22.imprint","IMPRINT",EDGE,{"derivedFrom":sQuery(id+"F22.wireOp",EDGE,"E76")}),1.0]])]});
            extrude(context, id + "F23", {"entities" : qUnion([Q0]), "operationType" : NewBodyOperationType.ADD, "depth" : 25.4 * mm});
        }
        {
            var Q0;
            {var subQ0=sQuery(id+"F0.wireOp",EDGE,"E0.rect.bottom");var subQ1=sQuery(id+"F0.wireOp",EDGE,"E0.rect.right");var subQ2=makeQuery(id+"F1.opExtrude","SWEPT_EDGE",EDGE,{"disambiguationData":[OSD([subQ0,subQ1])]});Q0=makeQuery(id+"F23.boolean.opBoolean","MERGE",FACE,{"derivedFrom":[makeQuery(id+"F9.opExtrude","SWEPT_FACE",FACE,{"disambiguationData":[OSD([subQ0,subQ1]),TDD([makeQuery(id+"F6.imprint","IMPRINT",EDGE,{"disambiguationData":[TD([[makeQuery(id+"F6.imprint","INTERSECT",VERTEX,{"derivedFrom":[subQ2,makeQuery(id+"F1.opExtrude","CAP_EDGE",EDGE,{"disambiguationData":[OSD([subQ1])],"isStart":false})]}),-1.0]])],"derivedFrom":subQ2})])]}),makeQuery(id+"F12.opExtrude","SWEPT_FACE",FACE,{"disambiguationData":[OSD([subQ0])]}),makeQuery(id+"F23.opExtrude","SWEPT_FACE",FACE,{"disambiguationData":[OSD([sQuery(id+"F22.wireOp",EDGE,"E76")])]})]});}
            var sketch = newSketch(context, id + "F24", { "sketchPlane" : qUnion([Q0])});
            skLineSegment(sketch, "E82", {"start": v(50.8, 76.2) * mm, "end": v(-76.2, 76.2) * mm});
            skLineSegment(sketch, "E83", {"start": v(-76.2, 76.2) * mm, "end": v(-76.2, 43.06) * mm});
            skLineSegment(sketch, "E84", {"start": v(-76.2, 43.06) * mm, "end": v(-50.8, 43.06) * mm});
            skLineSegment(sketch, "E85", {"start": v(-50.8, 43.06) * mm, "end": v(-50.8, 50.8) * mm});
            skLineSegment(sketch, "E86", {"start": v(-50.8, 50.8) * mm, "end": v(50.8, 50.8) * mm});
            skLineSegment(sketch, "E87", {"start": v(50.8, 50.8) * mm, "end": v(50.8, 76.2) * mm});
            skSolve(sketch);
        }
        {
            var Q0;
            Q0=makeQuery(id+"F24.imprint","IMPRINT",FACE,{"disambiguationData":[TD([[makeQuery(id+"F24.imprint","IMPRINT",EDGE,{"derivedFrom":sQuery(id+"F24.wireOp",EDGE,"E82")}),1.0]])]});
            extrude(context, id + "F25", {"entities" : qUnion([Q0]), "operationType" : NewBodyOperationType.ADD, "depth" : 25.4 * mm});
        }
        {
            var Q0;
            {var subQ0=sQuery(id+"F0.wireOp",EDGE,"E0.rect.top");var subQ1=sQuery(id+"F0.wireOp",EDGE,"E0.rect.right");var subQ2=makeQuery(id+"F1.opExtrude","SWEPT_EDGE",EDGE,{"disambiguationData":[OSD([subQ0,subQ1])]});var subQ4=makeQuery(id+"F1.opExtrude","CAP_EDGE",EDGE,{"disambiguationData":[OSD([subQ1])],"isStart":true});var subQ5=makeQuery(id+"F1.opExtrude","CAP_EDGE",EDGE,{"disambiguationData":[OSD([subQ1])],"isStart":false});var subQ11=sQuery(id+"F0.wireOp",EDGE,"E0.rect.left");var subQ12=makeQuery(id+"F1.opExtrude","SWEPT_EDGE",EDGE,{"disambiguationData":[OSD([subQ0,subQ11])]});var subQ24=makeQuery(id+"F1.opExtrude","SWEPT_FACE",FACE,{"disambiguationData":[OSD([subQ11])]});var subQ44=sQuery(id+"F14.wireOp",EDGE,"E71.right");var subQ45=sQuery(id+"F14.wireOp",EDGE,"E71.bottom");Q0=makeQuery(id+"F17.boolean.opBoolean","SPLIT",FACE,{"disambiguationData":[TD([makeQuery(id+"F15.opExtrude","SWEPT_FACE",FACE,{"disambiguationData":[OSD([subQ45])]})])],"derivedFrom":makeQuery(id+"F15.boolean.opBoolean","MERGE",FACE,{"derivedFrom":[makeQuery(id+"F11.boolean.opBoolean","MERGE",FACE,{"derivedFrom":[makeQuery(id+"F10.boolean.opBoolean","SPLIT",FACE,{"disambiguationData":[TD([subQ24])],"derivedFrom":makeQuery(id+"F9.boolean.opBoolean","MERGE",FACE,{"derivedFrom":[makeQuery(id+"F1.opExtrude","SWEPT_FACE",FACE,{"disambiguationData":[OSD([subQ0])]}),makeQuery(id+"F9.opExtrude","SWEPT_FACE",FACE,{"disambiguationData":[OSD([subQ0,subQ1]),TDD([makeQuery(id+"F6.imprint","IMPRINT",EDGE,{"disambiguationData":[TD([[makeQuery(id+"F6.imprint","INTERSECT",VERTEX,{"derivedFrom":[subQ2,subQ4]}),1.0]])],"derivedFrom":subQ2})])]}),makeQuery(id+"F9.opExtrude","SWEPT_FACE",FACE,{"disambiguationData":[OSD([subQ0,subQ1]),TDD([makeQuery(id+"F6.imprint","IMPRINT",EDGE,{"disambiguationData":[TD([[makeQuery(id+"F6.imprint","INTERSECT",VERTEX,{"derivedFrom":[subQ2,subQ5]}),-1.0]])],"derivedFrom":subQ2})])]})]})}),makeQuery(id+"F11.opExtrude","SWEPT_FACE",FACE,{"disambiguationData":[OSD([subQ0,subQ11]),TDD([makeQuery(id+"F3.imprint","IMPRINT",EDGE,{"disambiguationData":[TD([[makeQuery(id+"F3.imprint","INTERSECT",VERTEX,{"derivedFrom":[subQ12,sQuery(id+"F3.wireOp",EDGE,"E18")]}),-1.0]])],"derivedFrom":subQ12})])]})]}),makeQuery(id+"F13.opExtrude","SWEPT_FACE",FACE,{"disambiguationData":[OSD([subQ0])]}),makeQuery(id+"F15.opExtrude","SWEPT_FACE",FACE,{"disambiguationData":[OSD([subQ44])]})]})});}
            var sketch = newSketch(context, id + "F26", { "sketchPlane" : qUnion([Q0])});
            skLineSegment(sketch, "E88.bottom", {"start": v(76.2, -76.2) * mm, "end": v(-50.8, -76.2) * mm});
            skLineSegment(sketch, "E88.top", {"start": v(76.2, -50.8) * mm, "end": v(-50.8, -50.8) * mm});
            skLineSegment(sketch, "E88.left", {"start": v(76.2, -76.2) * mm, "end": v(76.2, -50.8) * mm});
            skLineSegment(sketch, "E88.right", {"start": v(-50.8, -76.2) * mm, "end": v(-50.8, -50.8) * mm});
            skSolve(sketch);
        }
        {
            var Q0;
            Q0=makeQuery(id+"F26.imprint","IMPRINT",FACE,{"disambiguationData":[TD([[makeQuery(id+"F26.imprint","IMPRINT",EDGE,{"derivedFrom":sQuery(id+"F26.wireOp",EDGE,"E88.bottom")}),1.0]])]});
            extrude(context, id + "F27", {"entities" : qUnion([Q0]), "operationType" : NewBodyOperationType.ADD, "depth" : 25.4 * mm});
        }
        {
            var Q0;
            {var subQ0=sQuery(id+"F0.wireOp",EDGE,"E0.rect.left");var subQ1=makeQuery(id+"F1.opExtrude","CAP_EDGE",EDGE,{"disambiguationData":[OSD([subQ0])],"isStart":true});Q0=makeQuery(id+"F13.opExtrude","SWEPT_FACE",FACE,{"disambiguationData":[OSD([subQ0]),TDD([makeQuery(id+"F5.imprint","IMPRINT",EDGE,{"disambiguationData":[TD([[makeQuery(id+"F5.imprint","INTERSECT",VERTEX,{"derivedFrom":[makeQuery(id+"F1.opExtrude","CAP_EDGE",EDGE,{"disambiguationData":[OSD([sQuery(id+"F0.wireOp",EDGE,"E0.rect.bottom")])],"isStart":true}),subQ1]}),-1.0]])],"derivedFrom":subQ1})])]});}
            var sketch = newSketch(context, id + "F28", { "sketchPlane" : qUnion([Q0])});
            skLineSegment(sketch, "E89.bottom", {"start": v(-50.8, -76.2) * mm, "end": v(0, -76.2) * mm});
            skLineSegment(sketch, "E89.top", {"start": v(-50.8, -50.8) * mm, "end": v(0, -50.8) * mm});
            skLineSegment(sketch, "E89.left", {"start": v(-50.8, -76.2) * mm, "end": v(-50.8, -50.8) * mm});
            skLineSegment(sketch, "E89.right", {"start": v(0, -76.2) * mm, "end": v(0, -50.8) * mm});
            skSolve(sketch);
        }
        {
            var Q0;
            Q0=makeQuery(id+"F28.imprint","IMPRINT",FACE,{"disambiguationData":[TD([[makeQuery(id+"F28.imprint","IMPRINT",EDGE,{"derivedFrom":sQuery(id+"F28.wireOp",EDGE,"E89.bottom")}),1.0]])]});
            extrude(context, id + "F29", {"entities" : qUnion([Q0]), "operationType" : NewBodyOperationType.ADD, "depth" : 25.4 * mm});
        }
        {
            var Q0;
            {var subQ0=sQuery(id+"F0.wireOp",EDGE,"E0.rect.bottom");var subQ1=sQuery(id+"F0.wireOp",EDGE,"E0.rect.left");var subQ2=makeQuery(id+"F1.opExtrude","CAP_EDGE",EDGE,{"disambiguationData":[OSD([subQ0])],"isStart":true});Q0=makeQuery(id+"F29.boolean.opBoolean","MERGE",FACE,{"derivedFrom":[makeQuery(id+"F11.opExtrude","SWEPT_FACE",FACE,{"disambiguationData":[OSD([subQ0,subQ1])]}),makeQuery(id+"F13.opExtrude","SWEPT_FACE",FACE,{"disambiguationData":[OSD([subQ0]),TDD([makeQuery(id+"F5.imprint","IMPRINT",EDGE,{"disambiguationData":[TD([[makeQuery(id+"F5.imprint","INTERSECT",VERTEX,{"derivedFrom":[subQ2,makeQuery(id+"F1.opExtrude","CAP_EDGE",EDGE,{"disambiguationData":[OSD([subQ1])],"isStart":true})]}),-1.0]])],"derivedFrom":subQ2})])]}),makeQuery(id+"F29.opExtrude","SWEPT_FACE",FACE,{"disambiguationData":[OSD([sQuery(id+"F28.wireOp",EDGE,"E89.left")])]})]});}
            var sketch = newSketch(context, id + "F30", { "sketchPlane" : qUnion([Q0])});
            skLineSegment(sketch, "E90", {"start": v(30.44, -76.2) * mm, "end": v(30.44, -50.8) * mm});
            skLineSegment(sketch, "E91", {"start": v(30.44, -50.8) * mm, "end": v(50.8, -50.8) * mm});
            skLineSegment(sketch, "E92", {"start": v(50.8, -50.8) * mm, "end": v(50.8, 50.8) * mm});
            skLineSegment(sketch, "E93", {"start": v(50.8, 50.8) * mm, "end": v(76.2, 50.8) * mm});
            skLineSegment(sketch, "E94", {"start": v(76.2, 50.8) * mm, "end": v(76.2, -76.2) * mm});
            skLineSegment(sketch, "E95", {"start": v(76.2, -76.2) * mm, "end": v(30.44, -76.2) * mm});
            skSolve(sketch);
        }
        {
            var Q0;
            Q0=makeQuery(id+"F30.imprint","IMPRINT",FACE,{"disambiguationData":[TD([[makeQuery(id+"F30.imprint","IMPRINT",EDGE,{"derivedFrom":sQuery(id+"F30.wireOp",EDGE,"E90")}),-1.0]])]});
            extrude(context, id + "F31", {"entities" : qUnion([Q0]), "operationType" : NewBodyOperationType.ADD, "depth" : 25.4 * mm});
        }
        {
            var Q0;
            {var subQ0=sQuery(id+"F0.wireOp",EDGE,"E0.rect.bottom");var subQ1=sQuery(id+"F0.wireOp",EDGE,"E0.rect.top");var subQ2=sQuery(id+"F0.wireOp",EDGE,"E0.rect.left");var subQ3=sQuery(id+"F0.wireOp",EDGE,"E0.rect.right");var subQ4=makeQuery(id+"F1.opExtrude","CAP_FACE",FACE,{"disambiguationData":[OSD([subQ0,subQ1,subQ2,subQ3])],"isStart":false});var subQ5=makeQuery(id+"F1.opExtrude","CAP_EDGE",EDGE,{"disambiguationData":[OSD([subQ0])],"isStart":false});var subQ6=makeQuery(id+"F8.opExtrude","SWEPT_FACE",FACE,{"disambiguationData":[OSD([subQ0]),TDD([makeQuery(id+"F7.imprint","IMPRINT",EDGE,{"derivedFrom":subQ5})])]});var subQ7=makeQuery(id+"F9.opExtrude","SWEPT_FACE",FACE,{"disambiguationData":[OSD([subQ3]),TDD([makeQuery(id+"F6.imprint","IMPRINT",EDGE,{"derivedFrom":makeQuery(id+"F1.opExtrude","CAP_EDGE",EDGE,{"disambiguationData":[OSD([subQ3])],"isStart":false})})])]});var subQ8=makeQuery(id+"F1.opExtrude","CAP_EDGE",EDGE,{"disambiguationData":[OSD([subQ1])],"isStart":false});var subQ11=makeQuery(id+"F10.opExtrude","SWEPT_FACE",FACE,{"disambiguationData":[OSD([subQ1]),TDD([makeQuery(id+"F4.imprint","IMPRINT",EDGE,{"disambiguationData":[TD([[makeQuery(id+"F4.imprint","INTERSECT",VERTEX,{"derivedFrom":[subQ8,sQuery(id+"F4.wireOp",EDGE,"E19")]}),1.0]])],"derivedFrom":subQ8})])]});var subQ12=makeQuery(id+"F10.opExtrude","SWEPT_FACE",FACE,{"disambiguationData":[OSD([subQ1]),TDD([makeQuery(id+"F4.imprint","IMPRINT",EDGE,{"disambiguationData":[TD([[makeQuery(id+"F4.imprint","INTERSECT",VERTEX,{"derivedFrom":[subQ8,sQuery(id+"F4.wireOp",EDGE,"E20")]}),-1.0]])],"derivedFrom":subQ8})])]});var subQ13=makeQuery(id+"F1.opExtrude","CAP_EDGE",EDGE,{"disambiguationData":[OSD([subQ2])],"isStart":false});var subQ14=sQuery(id+"F3.wireOp",EDGE,"E13");var subQ15=makeQuery(id+"F11.opExtrude","SWEPT_FACE",FACE,{"disambiguationData":[OSD([subQ2]),TDD([makeQuery(id+"F3.imprint","IMPRINT",EDGE,{"disambiguationData":[TD([[makeQuery(id+"F3.imprint","INTERSECT",VERTEX,{"derivedFrom":[subQ13,subQ14]}),1.0]])],"derivedFrom":subQ13})])]});var subQ16=makeQuery(id+"F11.opExtrude","SWEPT_FACE",FACE,{"disambiguationData":[OSD([subQ2]),TDD([makeQuery(id+"F3.imprint","IMPRINT",EDGE,{"disambiguationData":[TD([[makeQuery(id+"F3.imprint","INTERSECT",VERTEX,{"derivedFrom":[subQ13,sQuery(id+"F3.wireOp",EDGE,"E9")]}),-1.0]])],"derivedFrom":subQ13})])]});Q0=makeQuery(id+"F31.boolean.opBoolean","MERGE",FACE,{"derivedFrom":[makeQuery(id+"F12.boolean.opBoolean","SPLIT",FACE,{"disambiguationData":[TD([makeQuery(id+"F11.opExtrude","SWEPT_FACE",FACE,{"disambiguationData":[OSD([subQ14])]})])],"derivedFrom":makeQuery(id+"F11.boolean.opBoolean","MERGE",FACE,{"derivedFrom":[makeQuery(id+"F10.boolean.opBoolean","MERGE",FACE,{"derivedFrom":[makeQuery(id+"F9.boolean.opBoolean","MERGE",FACE,{"derivedFrom":[makeQuery(id+"F8.boolean.opBoolean","MERGE",FACE,{"derivedFrom":[subQ4,subQ6]}),subQ7]}),subQ11,subQ12]}),subQ15,subQ16]})}),makeQuery(id+"F31.opExtrude","SWEPT_FACE",FACE,{"disambiguationData":[OSD([sQuery(id+"F30.wireOp",EDGE,"E93")])]})]});}
            var sketch = newSketch(context, id + "F32", { "sketchPlane" : qUnion([Q0])});
            skLineSegment(sketch, "E96.bottom", {"start": v(-76.2, 76.2) * mm, "end": v(-50.8, 76.2) * mm});
            skLineSegment(sketch, "E96.top", {"start": v(-76.2, 38.66) * mm, "end": v(-50.8, 38.66) * mm});
            skLineSegment(sketch, "E96.left", {"start": v(-76.2, 76.2) * mm, "end": v(-76.2, 38.66) * mm});
            skLineSegment(sketch, "E96.right", {"start": v(-50.8, 76.2) * mm, "end": v(-50.8, 38.66) * mm});
            skSolve(sketch);
        }
        {
            var Q0;
            Q0=makeQuery(id+"F32.imprint","IMPRINT",FACE,{"disambiguationData":[TD([[makeQuery(id+"F32.imprint","IMPRINT",EDGE,{"derivedFrom":sQuery(id+"F32.wireOp",EDGE,"E96.bottom")}),-1.0]])]});
            extrude(context, id + "F33", {"entities" : qUnion([Q0]), "operationType" : NewBodyOperationType.ADD, "depth" : 25.4 * mm});
        }
        {
            var Q0;
            {var subQ0=sQuery(id+"F0.wireOp",EDGE,"E0.rect.top");var subQ1=sQuery(id+"F0.wireOp",EDGE,"E0.rect.left");var subQ2=makeQuery(id+"F1.opExtrude","SWEPT_EDGE",EDGE,{"disambiguationData":[OSD([subQ0,subQ1])]});Q0=makeQuery(id+"F11.opExtrude","SWEPT_FACE",FACE,{"disambiguationData":[OSD([subQ0,subQ1]),TDD([makeQuery(id+"F3.imprint","IMPRINT",EDGE,{"disambiguationData":[TD([[makeQuery(id+"F3.imprint","INTERSECT",VERTEX,{"derivedFrom":[subQ2,makeQuery(id+"F1.opExtrude","CAP_EDGE",EDGE,{"disambiguationData":[OSD([subQ1])],"isStart":true})]}),1.0]])],"derivedFrom":subQ2})])]});}
            var sketch = newSketch(context, id + "F34", { "sketchPlane" : qUnion([Q0])});
            skLineSegment(sketch, "E97.bottom", {"start": v(-76.2, -50.8) * mm, "end": v(-50.8, -50.8) * mm});
            skLineSegment(sketch, "E97.top", {"start": v(-76.2, -21.8) * mm, "end": v(-50.8, -21.8) * mm});
            skLineSegment(sketch, "E97.left", {"start": v(-76.2, -50.8) * mm, "end": v(-76.2, -21.8) * mm});
            skLineSegment(sketch, "E97.right", {"start": v(-50.8, -50.8) * mm, "end": v(-50.8, -21.8) * mm});
            skSolve(sketch);
        }
        {
            var Q0;
            Q0=makeQuery(id+"F34.imprint","IMPRINT",FACE,{"disambiguationData":[TD([[makeQuery(id+"F34.imprint","IMPRINT",EDGE,{"derivedFrom":sQuery(id+"F34.wireOp",EDGE,"E97.bottom")}),1.0]])]});
            extrude(context, id + "F35", {"entities" : qUnion([Q0]), "operationType" : NewBodyOperationType.ADD, "depth" : 25.4 * mm});
        }
        {
            var Q0;
            {var subQ0=sQuery(id+"F0.wireOp",EDGE,"E0.rect.bottom");var subQ1=sQuery(id+"F0.wireOp",EDGE,"E0.rect.top");var subQ2=sQuery(id+"F0.wireOp",EDGE,"E0.rect.left");var subQ3=sQuery(id+"F0.wireOp",EDGE,"E0.rect.right");var subQ4=makeQuery(id+"F1.opExtrude","CAP_FACE",FACE,{"disambiguationData":[OSD([subQ0,subQ1,subQ2,subQ3])],"isStart":true});var subQ5=makeQuery(id+"F1.opExtrude","CAP_EDGE",EDGE,{"disambiguationData":[OSD([subQ0])],"isStart":true});var subQ6=makeQuery(id+"F1.opExtrude","SWEPT_EDGE",EDGE,{"disambiguationData":[OSD([subQ0,subQ2])]});var subQ7=makeQuery(id+"F8.opExtrude","SWEPT_FACE",FACE,{"disambiguationData":[OSD([subQ0]),TDD([makeQuery(id+"F7.imprint","IMPRINT",EDGE,{"disambiguationData":[TD([[makeQuery(id+"F7.imprint","INTERSECT",VERTEX,{"derivedFrom":[subQ5,sQuery(id+"F7.wireOp",EDGE,"E58")]}),1.0]])],"derivedFrom":subQ5})])]});var subQ8=makeQuery(id+"F8.opExtrude","SWEPT_FACE",FACE,{"disambiguationData":[OSD([subQ0]),TDD([makeQuery(id+"F7.imprint","IMPRINT",EDGE,{"disambiguationData":[TD([[makeQuery(id+"F7.imprint","INTERSECT",VERTEX,{"derivedFrom":[subQ5,sQuery(id+"F7.wireOp",EDGE,"E59")]}),-1.0]])],"derivedFrom":subQ5})])]});var subQ9=makeQuery(id+"F9.opExtrude","SWEPT_FACE",FACE,{"disambiguationData":[OSD([subQ3]),TDD([makeQuery(id+"F6.imprint","IMPRINT",EDGE,{"derivedFrom":makeQuery(id+"F1.opExtrude","CAP_EDGE",EDGE,{"disambiguationData":[OSD([subQ3])],"isStart":true})})])]});var subQ10=makeQuery(id+"F1.opExtrude","CAP_EDGE",EDGE,{"disambiguationData":[OSD([subQ1])],"isStart":true});var subQ11=makeQuery(id+"F10.opExtrude","SWEPT_FACE",FACE,{"disambiguationData":[OSD([subQ1]),TDD([makeQuery(id+"F4.imprint","IMPRINT",EDGE,{"derivedFrom":subQ10})])]});var subQ12=makeQuery(id+"F1.opExtrude","CAP_EDGE",EDGE,{"disambiguationData":[OSD([subQ2])],"isStart":true});var subQ14=makeQuery(id+"F11.opExtrude","SWEPT_FACE",FACE,{"disambiguationData":[OSD([subQ2]),TDD([makeQuery(id+"F3.imprint","IMPRINT",EDGE,{"disambiguationData":[TD([[makeQuery(id+"F3.imprint","INTERSECT",VERTEX,{"derivedFrom":[subQ6,subQ12]}),-1.0]])],"derivedFrom":subQ12})])]});var subQ15=sQuery(id+"F3.wireOp",EDGE,"E17");var subQ17=makeQuery(id+"F1.opExtrude","SWEPT_EDGE",EDGE,{"disambiguationData":[OSD([subQ1,subQ2])]});var subQ18=makeQuery(id+"F3.imprint","INTERSECT",VERTEX,{"derivedFrom":[subQ17,subQ12]});var subQ19=makeQuery(id+"F11.opExtrude","SWEPT_FACE",FACE,{"disambiguationData":[OSD([subQ2]),TDD([makeQuery(id+"F3.imprint","IMPRINT",EDGE,{"disambiguationData":[TD([[subQ18,1.0]])],"derivedFrom":subQ12})])]});var subQ21=sQuery(id+"F3.wireOp",EDGE,"E12");Q0=makeQuery(id+"F35.boolean.opBoolean","MERGE",FACE,{"derivedFrom":[makeQuery(id+"F13.boolean.opBoolean","SPLIT",FACE,{"disambiguationData":[TD([makeQuery(id+"F11.opExtrude","CAP_FACE",FACE,{"disambiguationData":[OSD([subQ1,subQ2,subQ21,subQ15])],"isStart":false})])],"derivedFrom":makeQuery(id+"F11.boolean.opBoolean","MERGE",FACE,{"derivedFrom":[makeQuery(id+"F10.boolean.opBoolean","MERGE",FACE,{"derivedFrom":[makeQuery(id+"F9.boolean.opBoolean","MERGE",FACE,{"derivedFrom":[makeQuery(id+"F8.boolean.opBoolean","MERGE",FACE,{"derivedFrom":[subQ4,subQ7,subQ8]}),subQ9]}),subQ11]}),subQ14,subQ19]})}),makeQuery(id+"F35.opExtrude","SWEPT_FACE",FACE,{"disambiguationData":[OSD([sQuery(id+"F34.wireOp",EDGE,"E97.bottom")])]})]});}
            extrude(context, id + "F36", {"entities" : qUnion([Q0]), "operationType" : NewBodyOperationType.ADD, "depth" : 25.4 * mm});
        }
        {
            var Q0;
            {var subQ0=sQuery(id+"F0.wireOp",EDGE,"E0.rect.left");var subQ1=sQuery(id+"F0.wireOp",EDGE,"E0.rect.top");var subQ2=makeQuery(id+"F1.opExtrude","SWEPT_EDGE",EDGE,{"disambiguationData":[OSD([subQ1,subQ0])]});var subQ5=sQuery(id+"F4.wireOp",EDGE,"E21");Q0=makeQuery(id+"F11.boolean.opBoolean","SPLIT",FACE,{"disambiguationData":[TD([makeQuery(id+"F10.opExtrude","SWEPT_FACE",FACE,{"disambiguationData":[OSD([subQ5])]})])],"derivedFrom":makeQuery(id+"F10.boolean.opBoolean","MERGE",FACE,{"derivedFrom":[makeQuery(id+"F8.boolean.opBoolean","MERGE",FACE,{"derivedFrom":[makeQuery(id+"F1.opExtrude","SWEPT_FACE",FACE,{"disambiguationData":[OSD([subQ0])]}),makeQuery(id+"F8.opExtrude","SWEPT_FACE",FACE,{"disambiguationData":[OSD([sQuery(id+"F0.wireOp",EDGE,"E0.rect.bottom"),subQ0])]})]}),makeQuery(id+"F10.opExtrude","SWEPT_FACE",FACE,{"disambiguationData":[OSD([subQ1,subQ0]),TDD([makeQuery(id+"F4.imprint","IMPRINT",EDGE,{"disambiguationData":[TD([[makeQuery(id+"F4.imprint","INTERSECT",VERTEX,{"derivedFrom":[subQ2,makeQuery(id+"F1.opExtrude","CAP_EDGE",EDGE,{"disambiguationData":[OSD([subQ1])],"isStart":true})]}),1.0]])],"derivedFrom":subQ2})])]}),makeQuery(id+"F10.opExtrude","SWEPT_FACE",FACE,{"disambiguationData":[OSD([subQ1,subQ0]),TDD([makeQuery(id+"F4.imprint","IMPRINT",EDGE,{"disambiguationData":[TD([[makeQuery(id+"F4.imprint","INTERSECT",VERTEX,{"derivedFrom":[subQ2,makeQuery(id+"F1.opExtrude","CAP_EDGE",EDGE,{"disambiguationData":[OSD([subQ1])],"isStart":false})]}),-1.0]])],"derivedFrom":subQ2})])]}),makeQuery(id+"F10.opExtrude","SWEPT_FACE",FACE,{"disambiguationData":[OSD([subQ1,subQ0]),TDD([makeQuery(id+"F4.imprint","IMPRINT",EDGE,{"disambiguationData":[TD([[makeQuery(id+"F4.imprint","INTERSECT",VERTEX,{"derivedFrom":[subQ2,subQ5]}),1.0]])],"derivedFrom":subQ2})])]})]})});}
            var sketch = newSketch(context, id + "F37", { "sketchPlane" : qUnion([Q0])});
            skLineSegment(sketch, "E98.bottom", {"start": v(50.8, 3.6) * mm, "end": v(76.2, 3.6) * mm});
            skLineSegment(sketch, "E98.top", {"start": v(50.8, 15.3) * mm, "end": v(76.2, 15.3) * mm});
            skLineSegment(sketch, "E98.left", {"start": v(50.8, 3.6) * mm, "end": v(50.8, 15.3) * mm});
            skLineSegment(sketch, "E98.right", {"start": v(76.2, 3.6) * mm, "end": v(76.2, 15.3) * mm});
            skSolve(sketch);
        }
        {
            var Q0;
            Q0=makeQuery(id+"F37.imprint","IMPRINT",FACE,{"disambiguationData":[TD([[makeQuery(id+"F37.imprint","IMPRINT",EDGE,{"derivedFrom":sQuery(id+"F37.wireOp",EDGE,"E98.bottom")}),-1.0]])]});
            extrude(context, id + "F38", {"entities" : qUnion([Q0]), "operationType" : NewBodyOperationType.ADD, "depth" : 25.4 * mm});
        }
        {
            var Q0;
            {var subQ0=sQuery(id+"F0.wireOp",EDGE,"E0.rect.top");var subQ1=makeQuery(id+"F1.opExtrude","CAP_EDGE",EDGE,{"disambiguationData":[OSD([subQ0])],"isStart":false});Q0=makeQuery(id+"F12.opExtrude","SWEPT_FACE",FACE,{"disambiguationData":[OSD([subQ0]),TDD([makeQuery(id+"F2.imprint","IMPRINT",EDGE,{"disambiguationData":[TD([[makeQuery(id+"F2.imprint","INTERSECT",VERTEX,{"derivedFrom":[subQ1,makeQuery(id+"F1.opExtrude","CAP_EDGE",EDGE,{"disambiguationData":[OSD([sQuery(id+"F0.wireOp",EDGE,"E0.rect.left")])],"isStart":false})]}),-1.0]])],"derivedFrom":subQ1})])]});}
            extrude(context, id + "F39", {"entities" : qUnion([Q0]), "operationType" : NewBodyOperationType.ADD, "depth" : 25.4 * mm});
        }
    });
